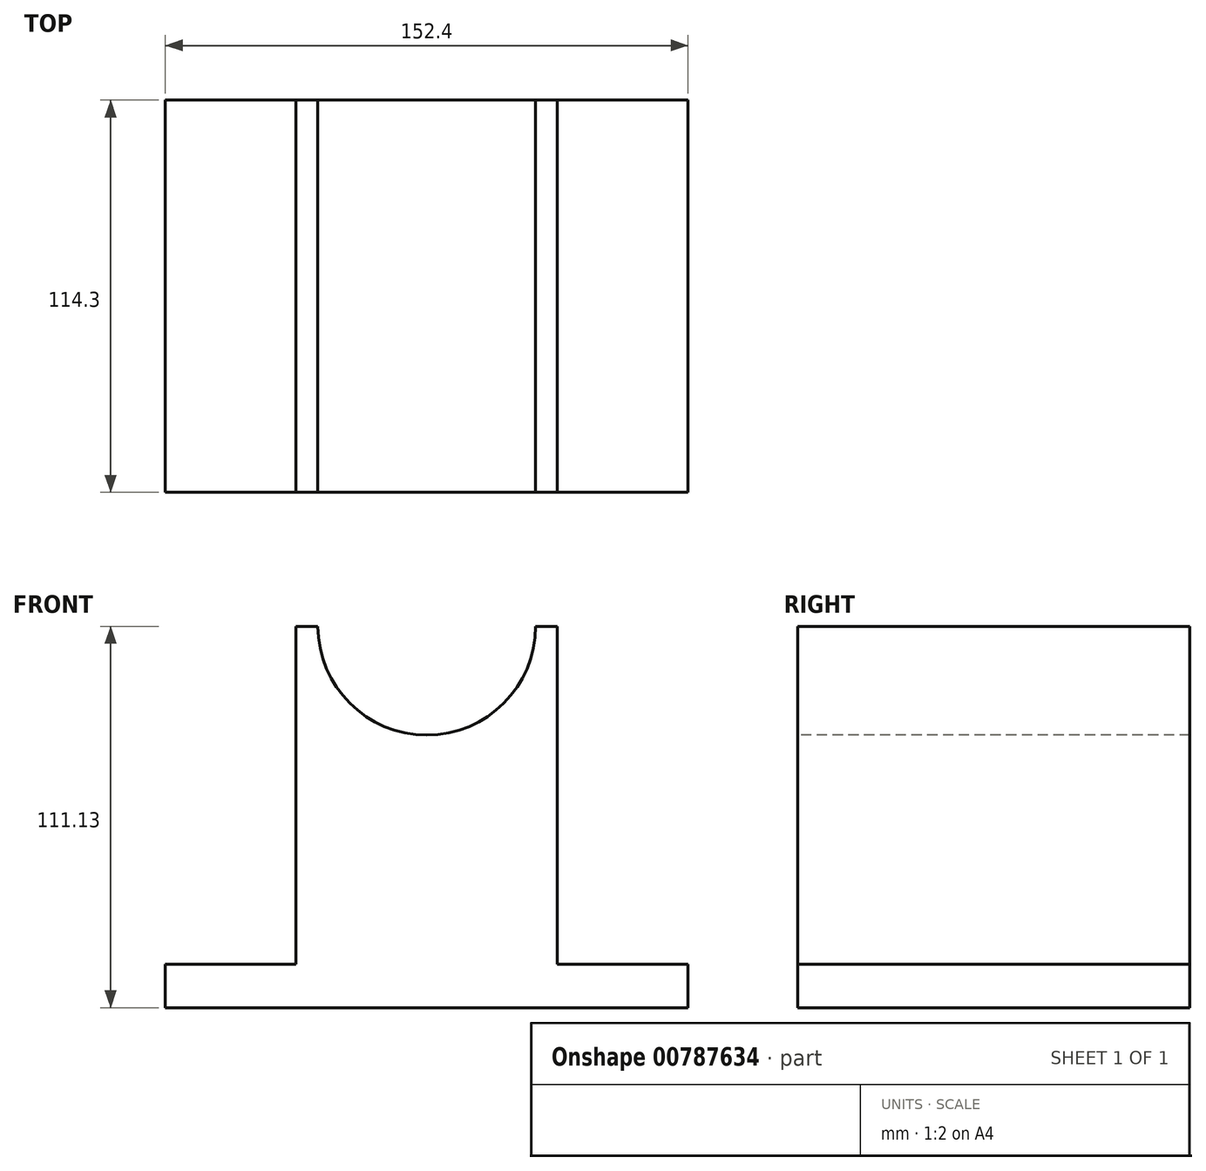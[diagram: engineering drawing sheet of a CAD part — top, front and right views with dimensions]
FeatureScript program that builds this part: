
annotation { "Feature Type Name" : "Feature", "Feature Type Description" : "" }
export const myFeature = defineFeature(function(context is Context, id is Id, definition is map)
    precondition{}
    {
        {
            var Q0;
            Q0=qCreatedBy(makeId("Front.planeOp"),FACE);
            var sketch = newSketch(context, id + "F0", { "sketchPlane" : qUnion([Q0])});
            skLineSegment(sketch, "E0", {"start": v(0, 0) * mm, "end": v(-38.1, 0) * mm});
            skLineSegment(sketch, "E1", {"start": v(-38.1, 0) * mm, "end": v(-38.1, 12.7) * mm});
            skLineSegment(sketch, "E2", {"start": v(-38.1, 12.7) * mm, "end": v(0, 12.7) * mm});
            skLineSegment(sketch, "E3", {"start": v(0, 12.7) * mm, "end": v(0, 111.13) * mm});
            skLineSegment(sketch, "E4", {"start": v(0, 111.13) * mm, "end": v(76.2, 111.13) * mm});
            skLineSegment(sketch, "E5", {"start": v(76.2, 111.13) * mm, "end": v(76.2, 12.7) * mm});
            skLineSegment(sketch, "E6", {"start": v(76.2, 12.7) * mm, "end": v(114.3, 12.7) * mm});
            skLineSegment(sketch, "E7", {"start": v(114.3, 12.7) * mm, "end": v(114.3, 0) * mm});
            skLineSegment(sketch, "E8", {"start": v(114.3, 0) * mm, "end": v(0, 0) * mm});
            skSolve(sketch);
        }
        {
            var Q0;
            Q0 = qSketchRegion(id + "F0", true);
            extrude(context, id + "F1", {"entities" : qUnion([Q0]), "depth" : 114.3 * mm, "offsetDistance" : 25.4 * mm});
        }
        {
            var Q0;
            Q0=makeQuery(id+"F1.opExtrude","CAP_FACE",FACE,{"disambiguationData":[OSD([sQuery(id+"F0.wireOp",EDGE,"E0"),sQuery(id+"F0.wireOp",EDGE,"E1"),sQuery(id+"F0.wireOp",EDGE,"E2"),sQuery(id+"F0.wireOp",EDGE,"E3"),sQuery(id+"F0.wireOp",EDGE,"E4"),sQuery(id+"F0.wireOp",EDGE,"E5"),sQuery(id+"F0.wireOp",EDGE,"E6"),sQuery(id+"F0.wireOp",EDGE,"E7"),sQuery(id+"F0.wireOp",EDGE,"E8")])],"isStart":false});
            var sketch = newSketch(context, id + "F2", { "sketchPlane" : qUnion([Q0])});
            skLineSegment(sketch, "E9", {"start": v(38.1, 111.13) * mm, "end": v(69.85, 111.13) * mm, "construction": true});
            skLineSegment(sketch, "E10", {"start": v(38.1, 111.13) * mm, "end": v(6.35, 111.13) * mm, "construction": true});
            skArc(sketch, "E11", {"start": v(6.35, 111.13) * mm, "mid": v(38.1, 79.43) * mm, "end": v(69.85, 111.13) * mm});
            skSolve(sketch);
        }
        {
            var Q0;
            Q0 = qSketchRegion(id + "F2", true);
            var Q1;
            {var subQ0=sQuery(id+"F2.wireOp",EDGE,"E11");Q1=makeQuery(id+"F2.imprint","IMPRINT",FACE,{"disambiguationData":[TD([[makeQuery(id+"F2.imprint","IMPRINT",EDGE,{"derivedFrom":subQ0}),1.0]])]});}
            extrude(context, id + "F3", {"entities" : qUnion([Q0, Q1]), "operationType" : NewBodyOperationType.REMOVE, "endBound" : BoundingType.THROUGH_ALL, "oppositeDirection" : true, "depth" : 25.4 * mm, "offsetDistance" : 25.4 * mm});
        }
    });
